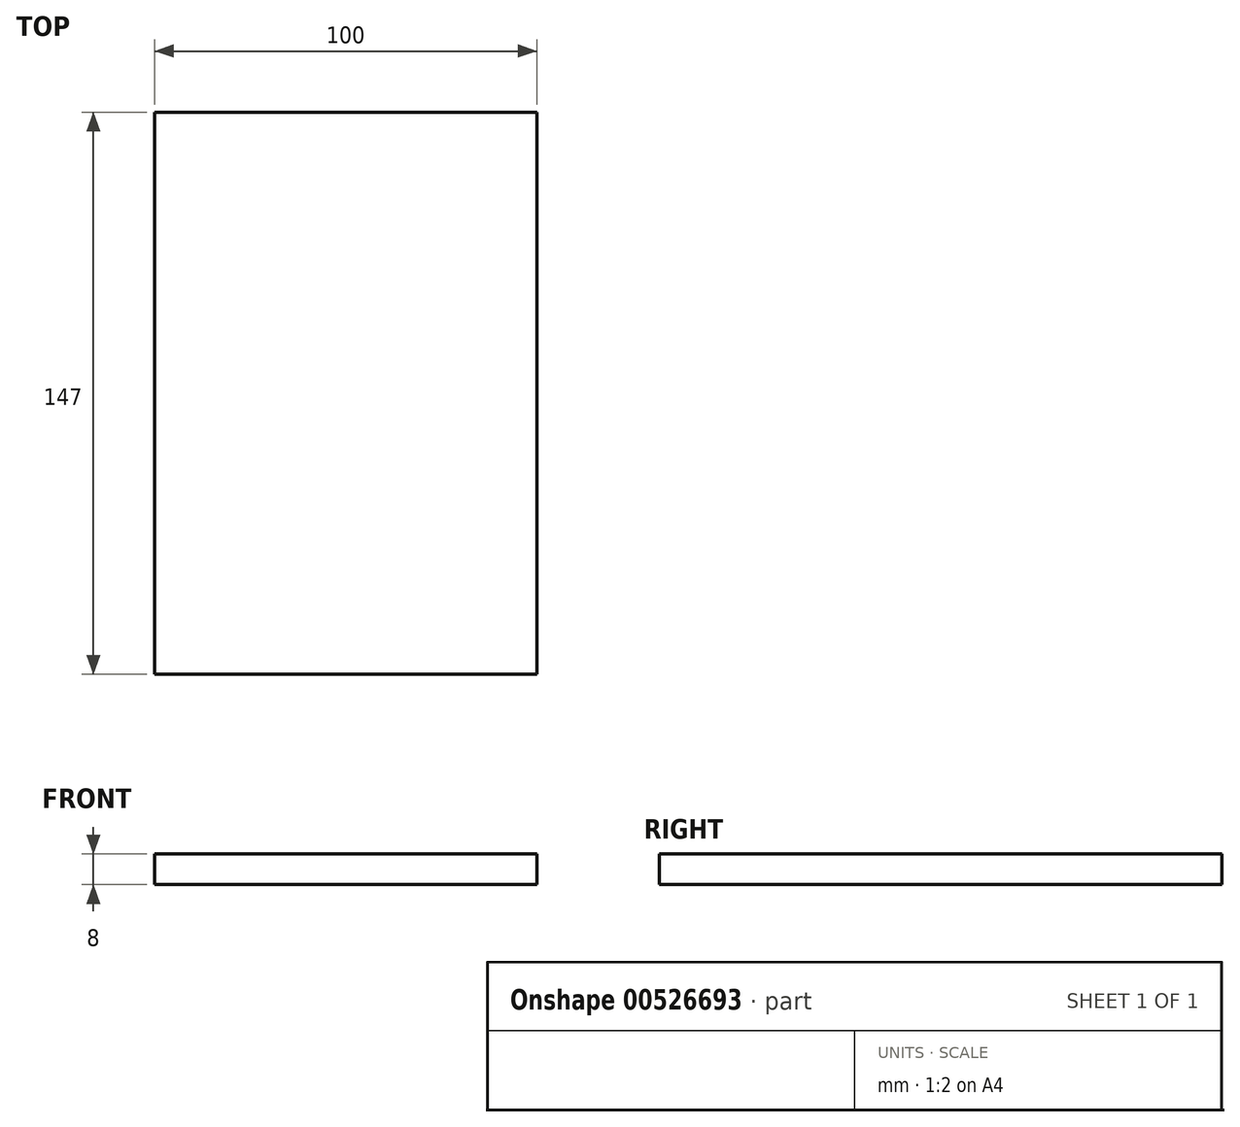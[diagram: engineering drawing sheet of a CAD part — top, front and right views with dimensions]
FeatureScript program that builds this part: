
annotation { "Feature Type Name" : "Feature", "Feature Type Description" : "" }
export const myFeature = defineFeature(function(context is Context, id is Id, definition is map)
    precondition{}
    {
        {
            var Q0;
            Q0=qCreatedBy(makeId("Top.planeOp"),FACE);
            var sketch = newSketch(context, id + "F0", { "sketchPlane" : qUnion([Q0])});
            skLineSegment(sketch, "E0.bottom", {"start": v(50, 73.5) * mm, "end": v(-50, 73.5) * mm});
            skLineSegment(sketch, "E0.top", {"start": v(50, -73.5) * mm, "end": v(-50, -73.5) * mm});
            skLineSegment(sketch, "E0.left", {"start": v(50, 73.5) * mm, "end": v(50, -73.5) * mm});
            skLineSegment(sketch, "E0.right", {"start": v(-50, 73.5) * mm, "end": v(-50, -73.5) * mm});
            skPoint(sketch, "E0.middle", {"position": v(0, 0) * mm});
            skSolve(sketch);
        }
        {
            var Q0;
            Q0 = qSketchRegion(id + "F0", true);
            extrude(context, id + "F1", {"entities" : qUnion([Q0]), "depth" : 8 * mm, "offsetDistance" : 25 * mm});
        }
    });
